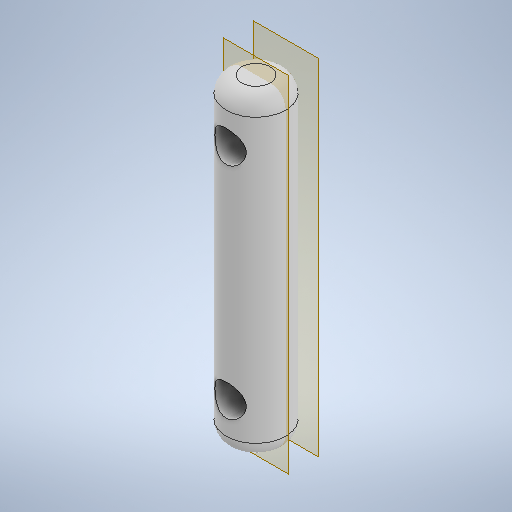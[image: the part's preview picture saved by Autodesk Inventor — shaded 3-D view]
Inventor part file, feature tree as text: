
AUTODESK INVENTOR PART (.ipt)
format: ipt  version: 2025.2 (Build 292293000, 293)  size: 269,824 bytes
history: native  units: mm
features: extrude x2, sketch x2, plane x1, fillet x1
ambient origin geometry x8: Origin, YZ Plane, XZ Plane, XY Plane, X Axis, Y Axis, Z Axis, Center Point
bodies: Solid1 (feature_tree)
feature tree (6):
  extrude  "Extrusion1"  Depth=100.0mm TaperAngle=0.0deg
  plane  "Work Plane1"
  extrude  "Extrusion2"  Depth=5.0mm
  fillet  "Fillet1"  Radius=35.0mm
  sketch  "Sketch1"  dims[d0=19.0mm d1=100.0mm d2=0.0mm]
  sketch  "Sketch2"  dims[d3=-9.5mm d4=35.0mm d5=35.0mm d6=10.0mm d7=10.0mm d8=20.0mm d9=0.0mm d10=5.0mm]
